# Revit family: Wall_Heaters-QMark-SSARWH_Smart_Series
name_source: partatom
category: Mechanical Equipment
revit_build: Autodesk Revit 2016 (Build: 20150220_1215(x64)
units: mm (PartAtom-declared; Revit-internal decimal feet)

## family parameters
Cut with Voids When Loaded = No
Host = Face
OmniClass Number = 23.75.70.17.34
OmniClass Title = Unit Heaters
Part Type = Normal
Room Calculation Point = No
Round Connector Dimension = Use Diameter
Shared = No

## types (4) — shared parameters
Apparent Load = 0 VA
Default Elevation = 4' - 0"
Description = Wall Heaters
Frequency = 60 Hz
Height = 1' - 6 1/4"
Manufacturer = Marley Engineered Products
Number of Poles = 1
Phase = 1
Product Documentation Link = https://www.marleymep.com
Product Name = SSAR Smart Series - Wall Heaters
Product Page URL = https://www.marleymep.com
Total Heating Capacity = 0.0 Btu/h
URL = http://www.marleymep.com
Width = 1' - 2 7/16"
zero-valued in all types: Power Factor

## per-type parameters (varying)
| type | Amps | Casing | Voltage | Watts |
| SSARWH1802 | 5 A | Metal - Berko - White Paint | 120 V | 540 W |
| SSARWH4808 | 9 A | Metal - Berko - Aluminum Finish | 208 V | 1800 W |
| SSARWH4804 | 8 A | Metal - Berko - White Paint | 240 V | 1800 W |
| SSARWH4807 | 7 A | Metal - Berko - White Paint | 277 V | 1800 W |

note: column(s) folded — value = type name in every type: Model

## geometry (parser evidence)
native form markers: Blend x3, Sweep x5
no freeform markers — native parametric forms only
